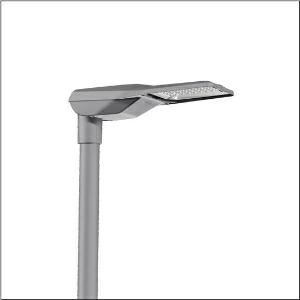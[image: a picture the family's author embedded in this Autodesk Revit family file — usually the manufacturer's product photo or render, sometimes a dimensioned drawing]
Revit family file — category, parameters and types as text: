
# Revit family: streetlight_sl_21_iq_mini___pl52_5xe2h41g08hb_e5d0
name_source: partatom
category: Lighting Fixtures
units: mm (PartAtom-declared; Revit-internal decimal feet)

## family parameters
Cut with Voids When Loaded = No
Host = Face
Light Source = No
Part Type = Normal
Room Calculation Point = No
Round Connector Dimension = Use Diameter
Shared = No

## types (1)
- --- (1 x LED, 9690 lm, 70.9 W, 4000K)
    Apparent Load = 71 VA
    CIE Flux Codes = 27 59 98 100 100
    Color Rendering = 70
    Color Temperature = 4000K
    Default Elevation = 1800 mm
    Description = Streetlight SL 21 iQ mini, mast luminaire, primary light control with lens, of PMMA, primary optical cover: cover, of toughened safety glass, transparent, light distribution: PL52, light emission: direct distribution, primary light characteristic: asymmetric, installation type: post-top, side-entry, LED, High Power LED, rated luminous flux: 9.690lm, luminous efficacy: 137lm/W, light colour: 740, colour temperature: 4000K, control: Street-Remote, Auto-Match, Temp-Guard, Lumen-Switch, Night-Set, Smart-Wire, Light-Fading, Desk-Remote (wireless, voltage-free reading and setting of iQ features in the workshop via application-optimized NFC function/RFID function), optimised constant luminous flux control (CLO 2.0), presetting dimming linear, mains connection: 220..240V, AC, 50/60Hz, start of lifetime: 71W, end of service life: 75W, reduction: 31W, luminaire housing, of diecast aluminium, powder-coated, Siteco® metallic grey (DB 702S), corrosivity category C5 mid according to DIN EN ISO 12944, please order mast flange separately, inclination adjustable: 0°, 5°, 10°, 15°, sealing non-destructively replaceable, multi-level sealing system, length: 628mm, width: 235mm, height: 110mm, mast flange for spigot size: 42mm (side-entry): 5XC10008XM4, 60/48mm (side-entry/post-top): 5XC10108XM2, 76/60mm (side-entry/post-top): 5XC10108XM1, protection rating (complete): IP66, insulation class (complete): insulation class II (safety insulation), certification: CE, ENEC, ENEC+, VDE, impact resistance: IK09, permissible operating ambient temperature for outdoor applications: -40..+50°C, standard-compliant lighting for roads and squares, packaging unit: 1 piece

Light Distribution: PL52
    Height = 110 mm
    Lamp = 1 x LED
    Lamp Light Flux = 9690 lm
    Lamp Power = 70.9 W
    Lamp count = 1
    Length = 625 mm
    Luminous efficacy = 137 lm/W
    Manufacturer = Siteco
    ModVariant = No
    Model = 5XE2H41G08HB
    Number of Poles = 1
    OnlyDefault = Yes
    Power Factor = 1
    Product Name = Streetlight SL 21 iQ mini | PL52
    Product group = mast luminaire | pylon top
    ProductGroupID = 6100
    Protection Class = Protection class II
    Protection Degree = IP 66
    RLX_Detail_Level = 1
    RLX_Emergency_Light_Flux = 0 lm
    RLX_Emergency_Type = 0
    RLX_Emergency_Type_DB = No
    RlxData = <blob elided: 101793 chars, md5=dae9f6cf>
    Socket = socket
    Standby Power = 0 W
    System Light Flux = 9690 lm
    System Power = 71 W
    Type Comments = factory setting: luminous flux: 100 % | dim-lin: 254 | 711 mA
    Type Image = l_1003519.jpg
    URL = http://relux.com
    VarID = @adj_108537
    Voltage = 0 V
    Weight = 0.00 kg
    Width = 234 mm

## geometry (parser evidence)
native form markers: Blend x4, Sweep x9
no freeform markers — native parametric forms only
